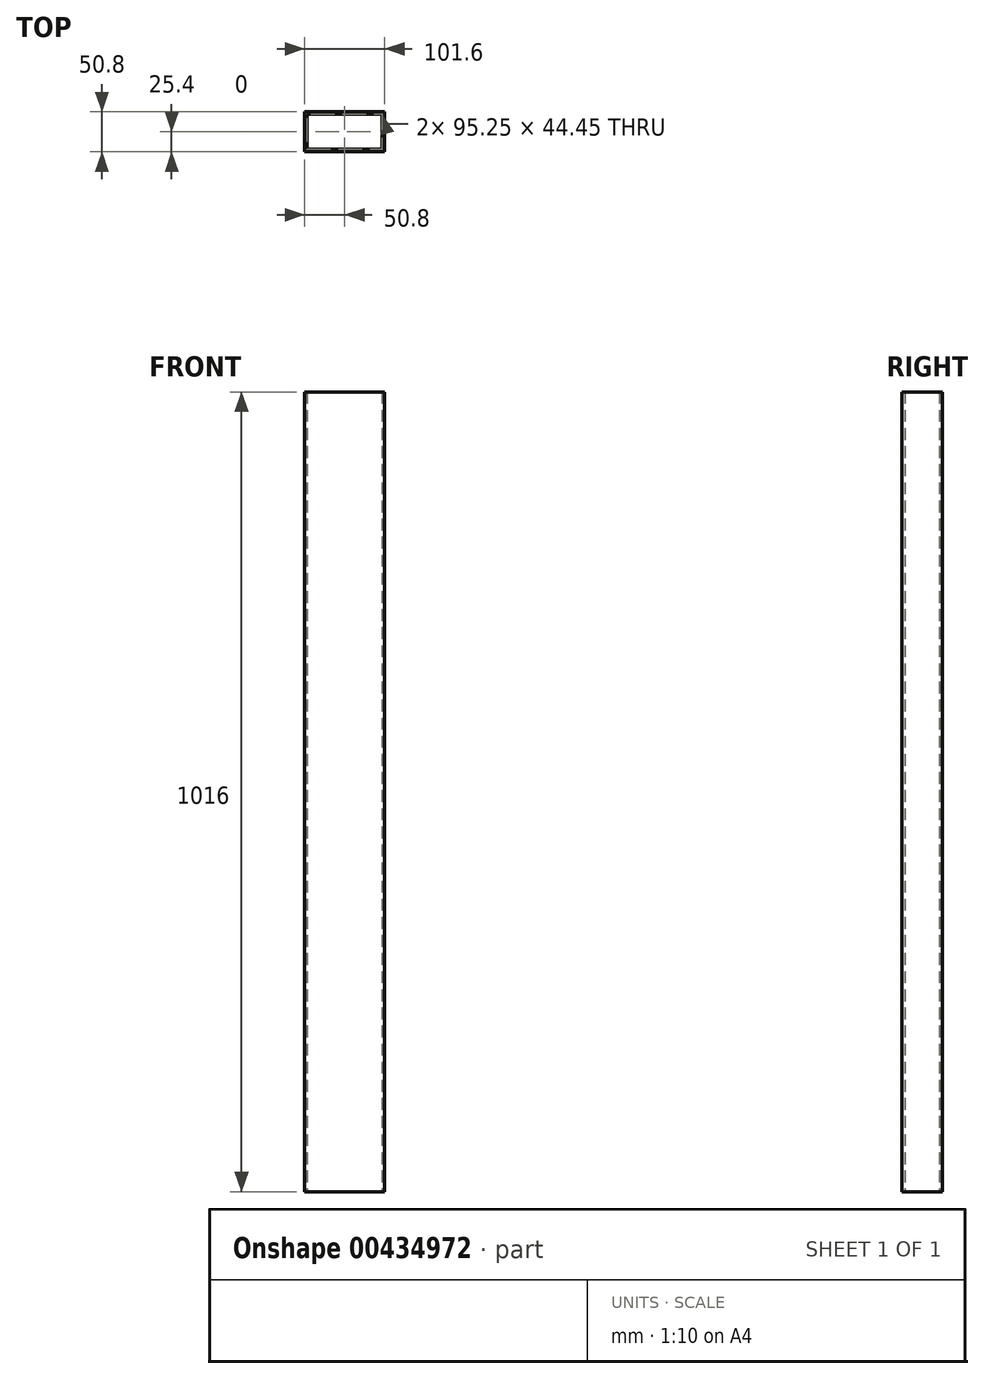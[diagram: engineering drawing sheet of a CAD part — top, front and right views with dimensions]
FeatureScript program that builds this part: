
annotation { "Feature Type Name" : "Feature", "Feature Type Description" : "" }
export const myFeature = defineFeature(function(context is Context, id is Id, definition is map)
    precondition{}
    {
        {
            var Q0;
            Q0=qCreatedBy(makeId("Top.planeOp"),FACE);
            var sketch = newSketch(context, id + "F0", { "sketchPlane" : qUnion([Q0])});
            skLineSegment(sketch, "E0.bottom", {"start": v(0, 0) * mm, "end": v(101.6, 0) * mm});
            skLineSegment(sketch, "E0.top", {"start": v(0, -50.8) * mm, "end": v(101.6, -50.8) * mm});
            skLineSegment(sketch, "E0.left", {"start": v(0, 0) * mm, "end": v(0, -50.8) * mm});
            skLineSegment(sketch, "E0.right", {"start": v(101.6, 0) * mm, "end": v(101.6, -50.8) * mm});
            skLineSegment(sketch, "E1.0", {"start": v(3.17, -3.18) * mm, "end": v(98.43, -3.18) * mm});
            skLineSegment(sketch, "E1.1", {"start": v(3.18, -3.18) * mm, "end": v(3.18, -47.63) * mm});
            skLineSegment(sketch, "E1.2", {"start": v(3.18, -47.63) * mm, "end": v(98.43, -47.63) * mm});
            skLineSegment(sketch, "E1.3", {"start": v(98.43, -3.18) * mm, "end": v(98.43, -47.63) * mm});
            skSolve(sketch);
        }
        {
            var Q0;
            Q0 = qSketchRegion(id + "F0", true);
            extrude(context, id + "F1", {"entities" : qUnion([Q0]), "depth" : 1016 * mm});
        }
    });
